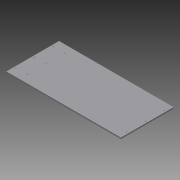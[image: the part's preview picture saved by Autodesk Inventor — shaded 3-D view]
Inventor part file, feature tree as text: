
AUTODESK INVENTOR PART (.ipt)
format: ipt  version: 2015 SP1 (Build 190203100, 203)  size: 102,400 bytes
history: native  units: mm
features: reference x4, sketch x2, extrude x1, hole x1
ambient origin geometry x8: Origin, YZ Plane, XZ Plane, XY Plane, X Axis, Y Axis, Z Axis, Center Point
bodies: Solid1 (feature_tree)
feature tree (8):
  extrude  "Extrusion1"  Depth=6.35mm
  hole  "Hole1"  [1 undecoded]
  sketch  "Sketch1"  dims[d0=6.35mm d1=0.0mm d2=20.0mm]
  reference  "Reference1"
  reference  "Reference2"
  reference  "Reference3"
  reference  "Reference4"
  sketch  "Sketch2"  dims[d3=80.0mm d4=80.0mm d5=20.0mm d6=140.0mm d7=4.5mm d8=6.0mm d9=8.0mm d10=4.0mm d11=90.0deg d12=8.0mm d13=20.594885mm]
note: 1 required parameter value undecoded (feature->parameter linkage not recoverable at this tier; creation-order binding heuristic only, values carry confidence <= 0.55)
